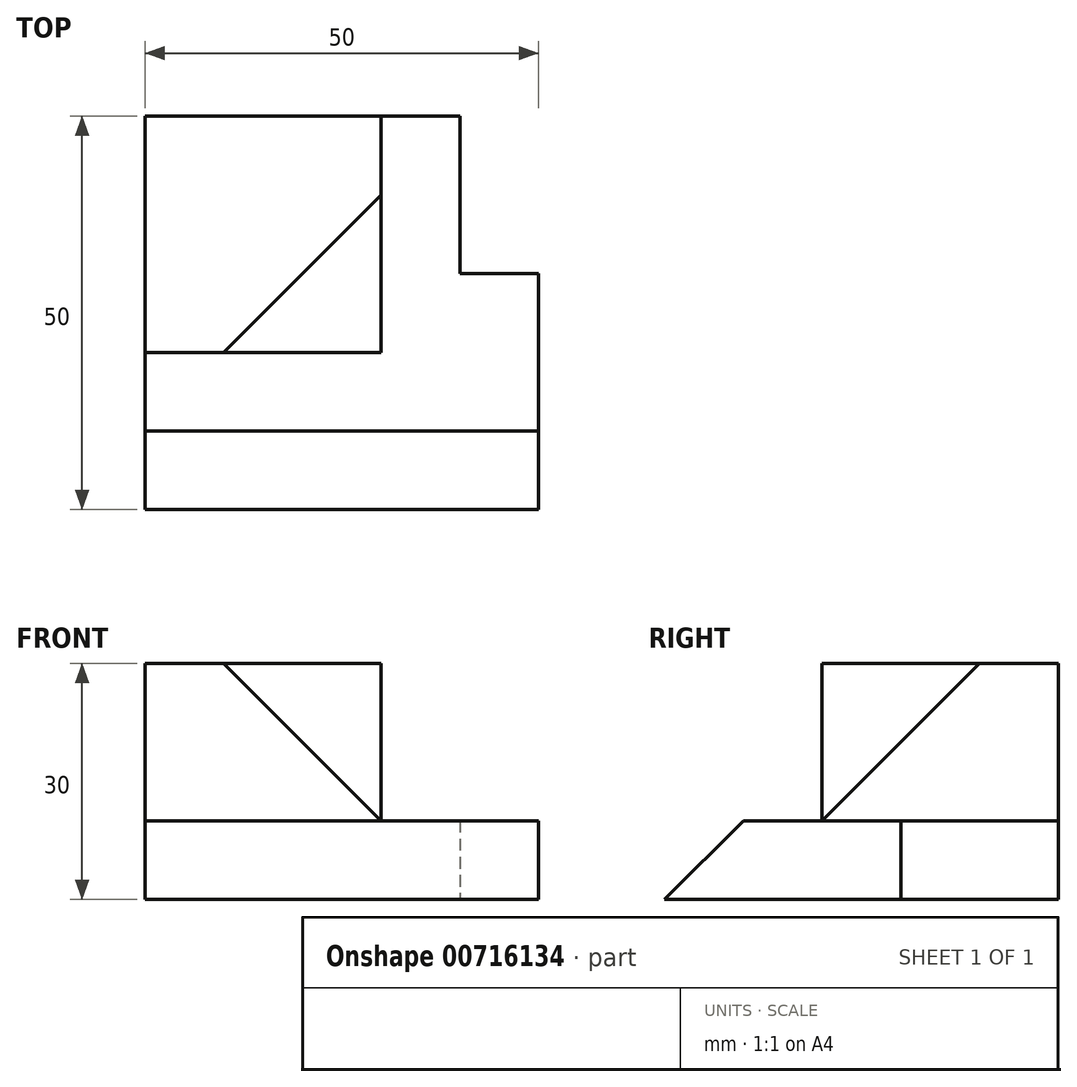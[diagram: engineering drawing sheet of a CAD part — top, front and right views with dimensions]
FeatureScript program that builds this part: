
annotation { "Feature Type Name" : "Feature", "Feature Type Description" : "" }
export const myFeature = defineFeature(function(context is Context, id is Id, definition is map)
    precondition{}
    {
        {
            var Q0;
            Q0=qCreatedBy(makeId("Top.planeOp"),FACE);
            var sketch = newSketch(context, id + "F0", { "sketchPlane" : qUnion([Q0])});
            skLineSegment(sketch, "E0.bottom", {"start": v(0, 0) * mm, "end": v(-50, 0) * mm});
            skLineSegment(sketch, "E0.top", {"start": v(-10, 50) * mm, "end": v(-50, 50) * mm});
            skLineSegment(sketch, "E0.left", {"start": v(0, 0) * mm, "end": v(0, 30) * mm});
            skLineSegment(sketch, "E0.right", {"start": v(-50, 0) * mm, "end": v(-50, 50) * mm});
            skLineSegment(sketch, "E1.top", {"start": v(0, 30) * mm, "end": v(-10, 30) * mm});
            skLineSegment(sketch, "E1.right", {"start": v(-10, 50) * mm, "end": v(-10, 30) * mm});
            skSolve(sketch);
        }
        {
            var Q0;
            Q0 = qSketchRegion(id + "F0", true);
            extrude(context, id + "F1", {"entities" : qUnion([Q0]), "depth" : 10 * mm, "offsetDistance" : 25 * mm});
        }
        {
            var Q0;
            Q0=makeQuery(id+"F1.opExtrude","CAP_EDGE",EDGE,{"disambiguationData":[OSD([sQuery(id+"F0.wireOp",EDGE,"E0.bottom")])],"isStart":false});
            chamfer(context, id + "F2", {"entities" : qUnion([Q0]), "width" : 10 * mm, "tangentPropagation" : true});
        }
        {
            var Q0;
            Q0=makeQuery(id+"F1.opExtrude","CAP_FACE",FACE,{"disambiguationData":[OSD([sQuery(id+"F0.wireOp",EDGE,"E0.bottom"),sQuery(id+"F0.wireOp",EDGE,"E0.top"),sQuery(id+"F0.wireOp",EDGE,"E0.left"),sQuery(id+"F0.wireOp",EDGE,"E0.right"),sQuery(id+"F0.wireOp",EDGE,"E1.top"),sQuery(id+"F0.wireOp",EDGE,"E1.right")])],"isStart":false});
            var sketch = newSketch(context, id + "F3", { "sketchPlane" : qUnion([Q0])});
            skLineSegment(sketch, "E2.bottom", {"start": v(-50, 50) * mm, "end": v(-20, 50) * mm});
            skLineSegment(sketch, "E2.top", {"start": v(-50, 20) * mm, "end": v(-20, 20) * mm});
            skLineSegment(sketch, "E2.left", {"start": v(-50, 50) * mm, "end": v(-50, 20) * mm});
            skLineSegment(sketch, "E2.right", {"start": v(-20, 50) * mm, "end": v(-20, 20) * mm});
            skSolve(sketch);
        }
        {
            var Q0;
            Q0 = qSketchRegion(id + "F3", true);
            extrude(context, id + "F4", {"entities" : qUnion([Q0]), "operationType" : NewBodyOperationType.ADD, "depth" : 20 * mm, "offsetDistance" : 25 * mm});
        }
        {
            var Q0;
            Q0=makeQuery(id+"F4.opExtrude","CAP_FACE",FACE,{"disambiguationData":[OSD([sQuery(id+"F3.wireOp",EDGE,"E2.bottom"),sQuery(id+"F3.wireOp",EDGE,"E2.top"),sQuery(id+"F3.wireOp",EDGE,"E2.left"),sQuery(id+"F3.wireOp",EDGE,"E2.right")])],"isStart":false});
            var sketch = newSketch(context, id + "F5", { "sketchPlane" : qUnion([Q0])});
            skLineSegment(sketch, "E3", {"start": v(-20, 20) * mm, "end": v(-40, 20) * mm});
            skLineSegment(sketch, "E4", {"start": v(-40, 20) * mm, "end": v(-20, 40) * mm});
            skLineSegment(sketch, "E5", {"start": v(-20, 40) * mm, "end": v(-20, 20) * mm});
            skSolve(sketch);
        }
        {
            var Q0;
            Q0=sQuery(id+"F5.wireOp",VERTEX,"E4.start");
            var Q1;
            Q1=sQuery(id+"F5.wireOp",VERTEX,"E5.start");
            var Q2;
            Q2=makeQuery(id+"F4.opExtrude","CAP_VERTEX",VERTEX,{"disambiguationData":[OSD([sQuery(id+"F3.wireOp",EDGE,"E2.top"),sQuery(id+"F3.wireOp",EDGE,"E2.right")])],"isStart":true});
            cPlane(context, id + "F6", {"entities" : qUnion([Q0, Q1, Q2]), "cplaneType" : CPlaneType.THREE_POINT, "offset" : 25 * mm, "width" : 150 * mm, "height" : 150 * mm});
        }
        {
            var Q0;
            Q0=makeQuery(id+"F5.imprint","IMPRINT",FACE,{"disambiguationData":[TD([[makeQuery(id+"F5.imprint","IMPRINT",EDGE,{"derivedFrom":sQuery(id+"F5.wireOp",EDGE,"E3")}),1.0]])]});
            var Q1;
            Q1=qCreatedBy(id+"F6.planeOp",FACE);
            extrude(context, id + "F7", {"entities" : qUnion([Q0]), "operationType" : NewBodyOperationType.REMOVE, "endBound" : BoundingType.UP_TO_SURFACE, "oppositeDirection" : true, "depth" : 25 * mm, "endBoundEntityFace" : qUnion([Q1]), "offsetDistance" : 25 * mm});
        }
    });
